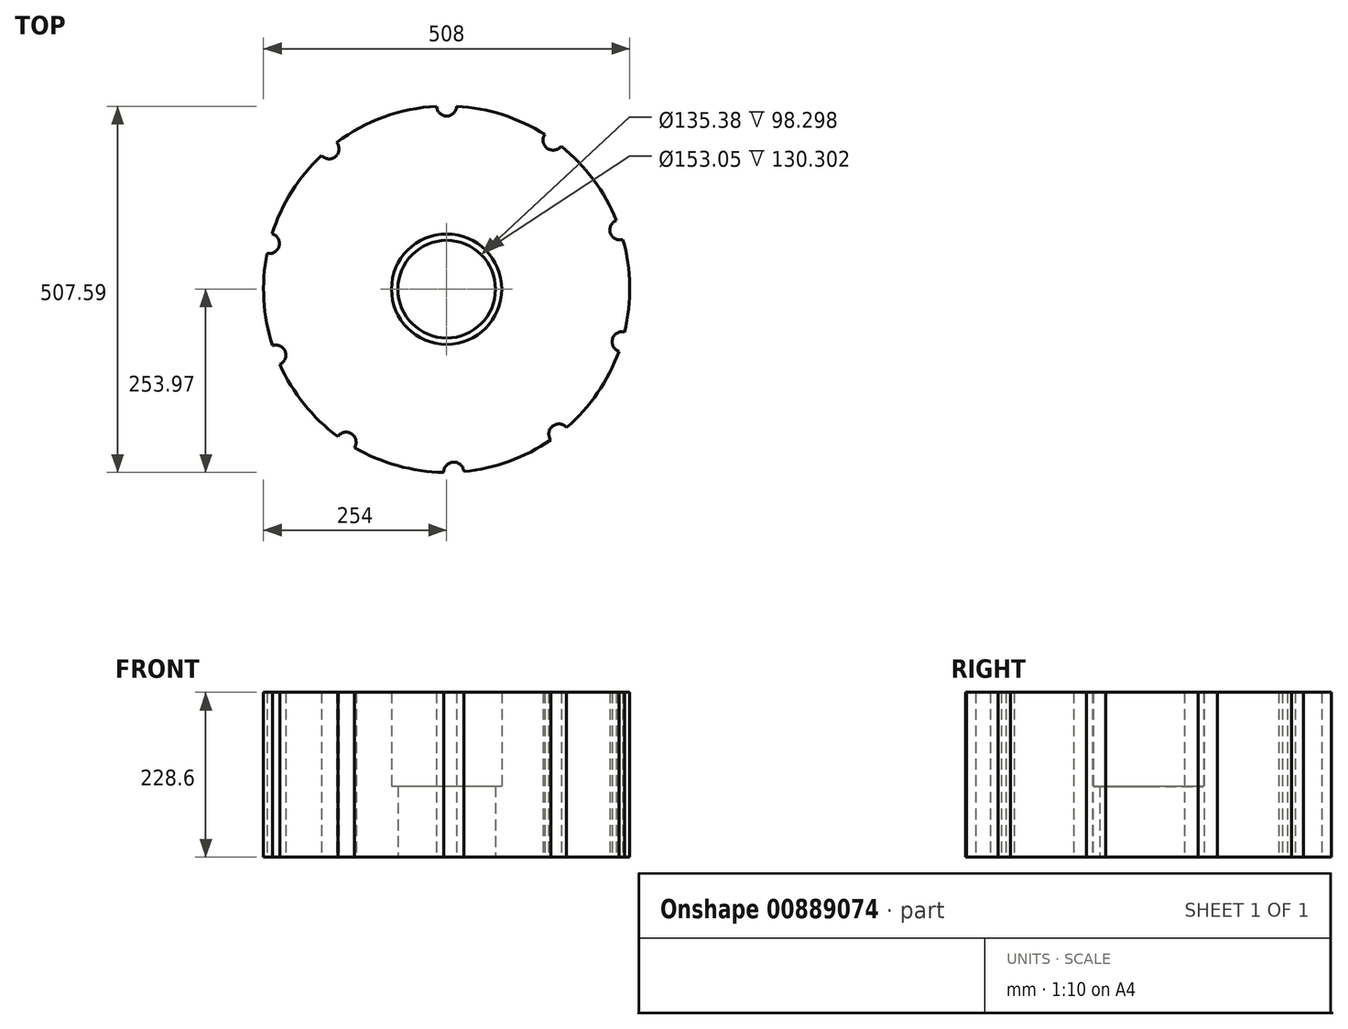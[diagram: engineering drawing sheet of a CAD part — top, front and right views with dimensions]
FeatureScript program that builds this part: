
annotation { "Feature Type Name" : "Feature", "Feature Type Description" : "" }
export const myFeature = defineFeature(function(context is Context, id is Id, definition is map)
    precondition{}
    {
        {
            var Q0;
            Q0=qCreatedBy(makeId("Top.planeOp"),FACE);
            var sketch = newSketch(context, id + "F0", { "sketchPlane" : qUnion([Q0])});
            skCircle(sketch, "E0.cCircle", {"center": v(0, 0) * mm, "radius": 126.11 * mm, "construction": true});
            skLineSegment(sketch, "E0.0", {"start": v(135.16, -54.2) * mm, "end": v(20.64, -144.15) * mm});
            skLineSegment(sketch, "E0.1", {"start": v(20.64, -144.15) * mm, "end": v(-114.52, -89.95) * mm});
            skLineSegment(sketch, "E0.2", {"start": v(-114.52, -89.95) * mm, "end": v(-135.16, 54.2) * mm});
            skLineSegment(sketch, "E0.3", {"start": v(-135.16, 54.2) * mm, "end": v(-20.64, 144.15) * mm});
            skLineSegment(sketch, "E0.4", {"start": v(-20.64, 144.15) * mm, "end": v(114.52, 89.95) * mm});
            skLineSegment(sketch, "E0.5", {"start": v(114.52, 89.95) * mm, "end": v(135.16, -54.2) * mm});
            skPoint(sketch, "E0.0.midPoint", {"position": v(77.9, -99.18) * mm});
            skCircle(sketch, "E1", {"center": v(0, 0) * mm, "radius": 67.7 * mm});
            skSolve(sketch);
        }
        {
            var Q0;
            Q0=makeQuery(id+"F0.imprint","IMPRINT",FACE,{"disambiguationData":[TD([[makeQuery(id+"F0.imprint","IMPRINT",EDGE,{"derivedFrom":sQuery(id+"F0.wireOp",EDGE,"E0.0")}),-1.0]])]});
            extrude(context, id + "F1", {"entities" : qUnion([Q0]), "depth" : 98.3 * mm, "offsetDistance" : 25.4 * mm});
        }
        {
            var Q0;
            Q0=qCreatedBy(makeId("Top.planeOp"),FACE);
            var sketch = newSketch(context, id + "F2", { "sketchPlane" : qUnion([Q0])});
            skCircle(sketch, "E2", {"center": v(0, 0) * mm, "radius": 254 * mm});
            skCircle(sketch, "E3", {"center": v(0, 254) * mm, "radius": 13.96 * mm});
            skCircle(sketch, "E4.1.0", {"center": v(147.7, 206.64) * mm, "radius": 13.96 * mm});
            skCircle(sketch, "E4.2.0", {"center": v(240.32, 82.23) * mm, "radius": 13.96 * mm});
            skCircle(sketch, "E4.3.0", {"center": v(243.33, -72.85) * mm, "radius": 13.96 * mm});
            skCircle(sketch, "E4.4.0", {"center": v(155.6, -200.76) * mm, "radius": 13.96 * mm});
            skCircle(sketch, "E4.5.0", {"center": v(9.85, -253.8) * mm, "radius": 13.96 * mm});
            skCircle(sketch, "E4.6.0", {"center": v(-139.58, -212.21) * mm, "radius": 13.96 * mm});
            skCircle(sketch, "E4.7.0", {"center": v(-236.95, -91.49) * mm, "radius": 13.96 * mm});
            skCircle(sketch, "E4.8.0", {"center": v(-245.97, 63.36) * mm, "radius": 13.96 * mm});
            skCircle(sketch, "E4.9.0", {"center": v(-163.27, 194.58) * mm, "radius": 13.96 * mm});
            skLineSegment(sketch, "E4.anchor1", {"start": v(0, 0) * mm, "end": v(0, 254) * mm, "construction": true});
            skLineSegment(sketch, "E4.anchor2", {"start": v(0, 0) * mm, "end": v(-163.27, 194.58) * mm, "construction": true});
            skCircle(sketch, "E5", {"center": v(0, 0) * mm, "radius": 76.52 * mm});
            skSolve(sketch);
        }
        {
            var Q0;
            Q0=makeQuery(id+"F2.imprint","IMPRINT",FACE,{"disambiguationData":[TD([[makeQuery(id+"F2.imprint","IMPRINT",EDGE,{"derivedFrom":sQuery(id+"F2.wireOp",EDGE,"E5")}),-1.0]])]});
            extrude(context, id + "F3", {"entities" : qUnion([Q0]), "operationType" : NewBodyOperationType.ADD, "depth" : 228.6 * mm, "offsetDistance" : 25.4 * mm});
        }
    });
